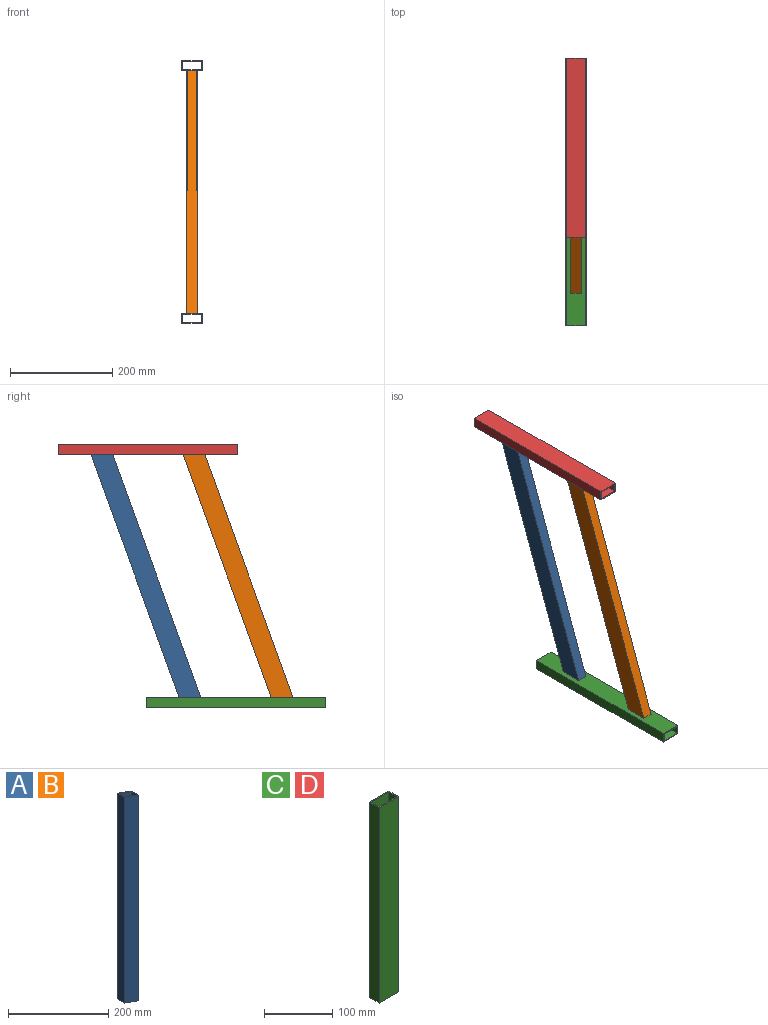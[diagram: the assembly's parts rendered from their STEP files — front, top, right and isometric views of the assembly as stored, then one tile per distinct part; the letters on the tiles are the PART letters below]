
ASSEMBLY  parts=4 mates=3
PART A: 10 faces, bbox 40x20x518 mm
  f0: plane 516.54x36mm, normal (0,1,0), area 18123.9mm2, adj f1,f3,f4,f5
  f1: plane 503.44x16mm, normal (-1,0,0), area 8055.1mm2, adj f0,f2,f4,f5
  f2: plane 516.54x36mm, normal (0,-1,0), area 18123.9mm2, adj f1,f3,f4,f5
  f3: plane 503.44x16mm, normal (1,0,0), area 8055.1mm2, adj f0,f2,f4,f5
  f4: plane 40x20mm, normal (0.34,0,0.94), area 238.4mm2, adj f0,f1,f2,f3,f6,f7,f8,f9
  f5: plane 40x20mm, normal (-0.34,0,-0.94), area 238.4mm2, adj f0,f1,f2,f3,f6,f7,f8,f9
  f6: plane 518x40mm, normal (0,-1,0), area 20137.6mm2, adj f4,f5,f7,f9
  f7: plane 503.44x20mm, normal (1,0,0), area 10068.8mm2, adj f4,f5,f6,f8
  f8: plane 518x40mm, normal (0,1,0), area 20137.6mm2, adj f4,f5,f7,f9
  f9: plane 503.44x20mm, normal (-1,0,0), area 10068.8mm2, adj f4,f5,f6,f8
PART B: same geometry as A
PART C: 10 faces, bbox 40x20x350 mm
  f0: plane 350x40mm, normal (0,1,0), area 14000mm2, adj f1,f7,f8,f9
  f1: plane 350x20mm, normal (-1,0,0), area 7000mm2, adj f0,f2,f8,f9
  f2: plane 350x40mm, normal (0,-1,0), area 14000mm2, adj f1,f7,f8,f9
  f3: plane 350x16mm, normal (1,0,0), area 5600mm2, adj f4,f6,f8,f9
  f4: plane 350x36mm, normal (0,-1,0), area 12600mm2, adj f3,f5,f8,f9
  f5: plane 350x16mm, normal (-1,0,0), area 5600mm2, adj f4,f6,f8,f9
  f6: plane 350x36mm, normal (0,1,0), area 12600mm2, adj f3,f5,f8,f9
  f7: plane 350x20mm, normal (1,0,0), area 7000mm2, adj f0,f2,f8,f9
  f8: plane 40x20mm, normal (0,0,1), area 224mm2, adj f0,f1,f2,f3,f4,f5,f6,f7
  f9: plane 40x20mm, normal (0,0,-1), area 224mm2, adj f0,f1,f2,f3,f4,f5,f6,f7
PART D: same geometry as C
PLACE A rot(axis=(-0.17,-0.17,-0.97),91.7deg) t=(-68,72.5,326.28)mm
PLACE B rot(axis=(-0.17,-0.17,-0.97),91.7deg) t=(-68,-107.5,326.28)mm
PLACE C rot(axis=(-1,0,0),90deg) t=(-68,-190.01,323.12)mm
PLACE D rot(axis=(-1,0,0),90deg) t=(-68,-17.83,816.2)mm
MATE fastened D.f0 <-> B.f4  axis (0,0,-1) through (-68,157.17,806.2)mm
MATE fastened A.f5 <-> C.f2  axis (0,0,-1) through (-68,74.99,333.12)mm
MATE fastened B.f5 <-> C.f2  axis (0,0,-1) through (-68,-105.01,333.12)mm
